# Revit family: VIESSMANN - Vitodens 200-W B2HF
name_source: partatom
category: Wyposażenie mechaniczne
revit_build: Autodesk Revit 2017 (Build: 20160720_1515(x64)
units: mm (PartAtom-declared; Revit-internal decimal feet)

## family parameters
Numer OmniClass = 23.75.10.11.14.14
Obiekt nadrzędny = Powierzchnia
Punkt obliczania pomieszczeń = Nie
Tnij formami wycięć po wczytaniu = Nie
Typ części = Normalny
Tytuł OmniClass = Condensing Boilers
Współdzielony = Nie
Wymiar okrągłego złącza = Użyj średnicy

## types (4) — shared parameters
Autor = www.archispace.pl
Bezpiecznik urządzenia = 6 A
Bezpiecznik wstępny = 16 A
Częstotliwość = 50 Hz
Domyślna rzędna = 1219 mm
Dop. ciśnienie robocze (PMS) = 300000.0 Pa
Dop. temperatura otoczenia - podczas eksploatacji = od +5 do +40 °C
Dop. temperatura otoczenia - podczas magazynowania i transportu = od -5 do +60 °C
Długość = 360 mm
Liczba biegunów = 1
Maks. temperatura cwu = 70 °C
Masa - bez wody grzewczej = 33.00 kg
Masa - z wodą grzewczą = 38.60 kg
Moduł RF - maks. moc nadawcza (częstotliwość Zigbee) = 10 dBm
Moduł RF - maks. moc nadawcza (częstotliwość sieci Wi-Fi) = 17 dBm
Moduł RF - napięcie zasilania = 24 V
Moduł RF - pobór mocy = 2 W
Moduł RF - zakres częstotliwości Zigbee = 2400 - 2483.5 MHz
Moduł RF - zakres częstotliwości sieci Wi-Fi = 2400 - 2483.5 MHz
NOx = Klasa 6
Napięcie znamionowe = 230 V
Numer identyfikacyjny produktu = CE-0085CT0017
Opis = Gazowy kocioł kondensacyjny
Opis indeksowy = CE-0085CT0017
Parametry spalin - maks. temperatura = 120 °C
Powrót z instalacji R = 3/4"
Powrót z podgrzewacza G = 3/4"
Producent = Viessmann Sp.z.o.o.
Przewód powietrza dolotowego = 100.00 mm
Przyłącze gazu R = 3/4"
Przyłącze spalin = 60 mm
Stopień ochrony = IP X4 według EN 60529
Szerokość = 450 mm  [stored 1.47638 ft]
URL = https://www.viessmann-projektant.pl
Ustawienie elektronicznego czujnika temperatury (TN) = 91 °C
Ustawienie elektronicznego ogranicznika temperatury = 110 °C
Viessmann Kolor 1 = Viessmann Kolor 1
Viessmann Kolor 2 = Viessmann Kolor 2
Viessmann Kolor 3 = Viessmann Kolor 3
Współczynnik mocy = 1
Wysokość = 700 mm
Zasilanie instalacji R = 3/4"
Zasilanie podgrzewacza G = 3/4"

## per-type parameters (varying)
| type | Moc nominalna | Model | Parametry przyłączeniowe (w odniesieniu do maks. obciążenia) dla gazu płynnego | Parametry przyłączeniowe (w odniesieniu do maks. obciążenia) dla gazu ziemnego E/GZ50/G20 | Parametry przyłączeniowe (w odniesieniu do maks. obciążenia) dla gazu ziemnego Lw/GZ41,5/G27 | Parametry spalin - masowe natężenie przepływu (przy podgrzewie cwu) gazu płynnego | Parametry spalin - masowe natężenie przepływu (przy podgrzewie cwu) gazu ziemnego | Parametry spalin - temperatura (przy podgrzewie cwu) | Pobór mocy elektrycznej | Przepływ maksymalny | Zakres znamionowej mocy cieplnej przy Tv/Tr 50/30°C - gaz płynny, gaz ziemny M | Zakres znamionowej mocy cieplnej przy Tv/Tr 50/30°C - gaz ziemny | Zakres znamionowej mocy cieplnej przy Tv/Tr 80/60°C - gaz płynny, gaz ziemny M | Zakres znamionowej mocy cieplnej przy Tv/Tr 80/60°C - gaz ziemny | Znamionowa moc cieplna przy podgrzewie cwu - gaz płynny, gaz ziemny M | Znamionowa moc cieplna przy podgrzewie cwu - gaz ziemny | Znamionowe obciążenie cieplne (Qn) - gaz płynny, gaz ziemny M | Znamionowe obciążenie cieplne (Qn) - gaz ziemny | Znamionowe obciążenie cieplne przy podgrzewie cwu (Qnw) |
| Vitodens 200-W B2HF 32kW | 32000 W | Gazowy kocioł kondensacyjny Vitodens 200-W B2HF 32kW / Gas-fired condensing boiler Vitodens 200-W B2HF 32kW | 2.32 kg/h | 3.168 m³/h | 3.672 m³/h | 53.9 g/s | 54.9 g/s | 72 °C | 92 W | 1.382 m³/h | 2.5 - 32.0 kW | 1.9 - 32.0 kW | 2.2 - 29.3 kW | 1.7 - 29.3 kW | 2.2 - 29.3 kW | 1.7 - 29.3 kW | 2.3 - 29.9 kW | 1.8 - 29.9 kW | 30 W |
| Vitodens 200-W B2HF 11kW | 11000 W | Gazowy kocioł kondensacyjny Vitodens 200-W B2HF 11kW / Gas-fired condensing boiler Vitodens 200-W B2HF 11kW | 1.38 kg/h | 1.872 m³/h | 2.196 m³/h | 30.1 g/s | 31.7 g/s | 64 °C | 37 W | 0.475 m³/h | 2.5 - 11.0 kW | 1.9 - 11.0 kW | 2.2 - 10.1 kW | 1.7 - 10.1 kW | 2.2 - 17.4 kW | 1.7 - 17.4 kW | 2.3 - 10.3 kW | 1.8 - 10.3 kW | 17800 W |
| Vitodens 200-W B2HF 19kW | 19000 W | Gazowy kocioł kondensacyjny Vitodens 200-W B2HF 19kW / Gas-fired condensing boiler Vitodens 200-W B2HF 19kW | 1.38 kg/h | 1.872 m³/h | 2.196 m³/h | 30.1 g/s | 31.7 g/s | 65 °C | 47 W | 0.821 m³/h | 2.5 - 19.0 kW | 1.9 - 19.0 kW | 2.2 - 17.4 kW | 1.7 - 17.4 kW | 2.2 - 17.4 kW | 1.7 - 17.4 kW | 2.3 - 17.8 kW | 1.8 - 17.8 kW | 18800 W |
| Vitodens 200-W B2HF 25kW | 25000 W | Gazowy kocioł kondensacyjny Vitodens 200-W B2HF 25kW / Gas-fired condensing boiler Vitodens 200-W B2HF 25kW | 1.82 kg/h | 2.484 m³/h | 2.880 m³/h | 41 g/s | 41.6 g/s | 67 °C | 68 W | 1.080 m³/h | 2.5 - 25.0 kW | 1.9 - 25.0 kW | 2.2 - 22.9 kW | 1.7 - 22.9 kW | 2.2 - 22.9 kW | 1.7 - 22.9 kW | 2.3 - 23.4 kW | 1.8 - 23.4 kW | 23400 W |

note: [stored X ft] marks values corroborated as IEEE doubles in the binary element streams (Revit-internal decimal feet)
